# Revit family: TSL.960
name_source: partatom
category: Generic Models
revit_build: Autodesk Revit 2018 (Build: 20170223_1515(x64)
units: mm (PartAtom-declared; Revit-internal decimal feet)

## family parameters
Can host rebar = No
Cut with Voids When Loaded = No
Host = Face
OmniClass Number = 23.45.55.14
OmniClass Title = Single Faucets
Part Type = Normal
Room Calculation Point = No
Round Connector Dimension = Use Diameter
Shared = No

## types (5) — shared parameters
AssetType = fixed
DocumentationInstallationGuide = www.thesplashlab.com
DocumentationLiterature = www.thesplashlab.com
DocumentationMaintenance = www.thesplashlab.com
DocumentationTechnical = www.thesplashlab.com
DurationUnit = Years
ExpectedLife = 2
Grade = 316AISI
Keynote = N13
Manufacturer = TheSplashLab
Mtrl_Grade = 316AISI
Mtrl_Material = stainless steel
NBSObjectName = Washroom_Accessories-TSL-960_Tap-THESPLASHLAB-Deck_Mounted
NBSReference = Pr_40_30_78_16
Product Documentation Link = www.thesplashlab.com
Product O&M Link = www.thesplashlab.com
Product Page Link = www.thesplashlab.com
Product Specification Link = www.thesplashlab.com
Type Comments = The Tap is made from AISI 304 type stainless steel in a brushed satin finish
URL = www.thesplashlab.com
Uniclass2 = Pr_40_30_78_16
Vent Connection = No
WarrantyDescription = 2 years from date of purchase
WarrantyDurationParts = 12
WarrantyDurationUnit = months
Waste Connection = No
_current revision = 1
material test = <By Category>
zero-valued in all types: Default Elevation, Mtrl_ExpectedLife, Mtrl_ReplacementCost, Mtrl_SerialNumber, Mtrl_TagNumber, Mtrl_WarrantyDurationLabor, Mtrl_WarrantyDurationParts, Mtrl_bimspec_guid, Mtrl_current revision, _BIMspec_GUID

## per-type parameters (varying)
| type | Assembly Code | Finish | Material | Model | TypeName | finish |
| TSL-947_steel |  | Brushed stainless steel finish | Brushed stainless steel finish | TSL-410 | TSL-410 | Brushed stainless steel finish |
| TSL-947_copper | E2010 | Brushed copper finish | Brushed copper finish | TSL-960 | TSL-960 | Brushed copper finish |
| TSL-947_black | E2010 | Brushed black finish | Brushed black finish | TSL-947BK | TSL-947BK | Brushed black finish |
| TSL-947_bronze | E2010 | Brushed bronze finish | Brushed bronze finish | TSL-947BZ | TSL-947BZ | Brushed bronze finish |
| TSL-947_brass | E2010 | Brushed brass finish | Brushed brass finish | TSL-947BR | TSL-947BR | Brushed brass finish |

## geometry (parser evidence)
native form markers: Blend x14, Sweep x5
no freeform markers — native parametric forms only
